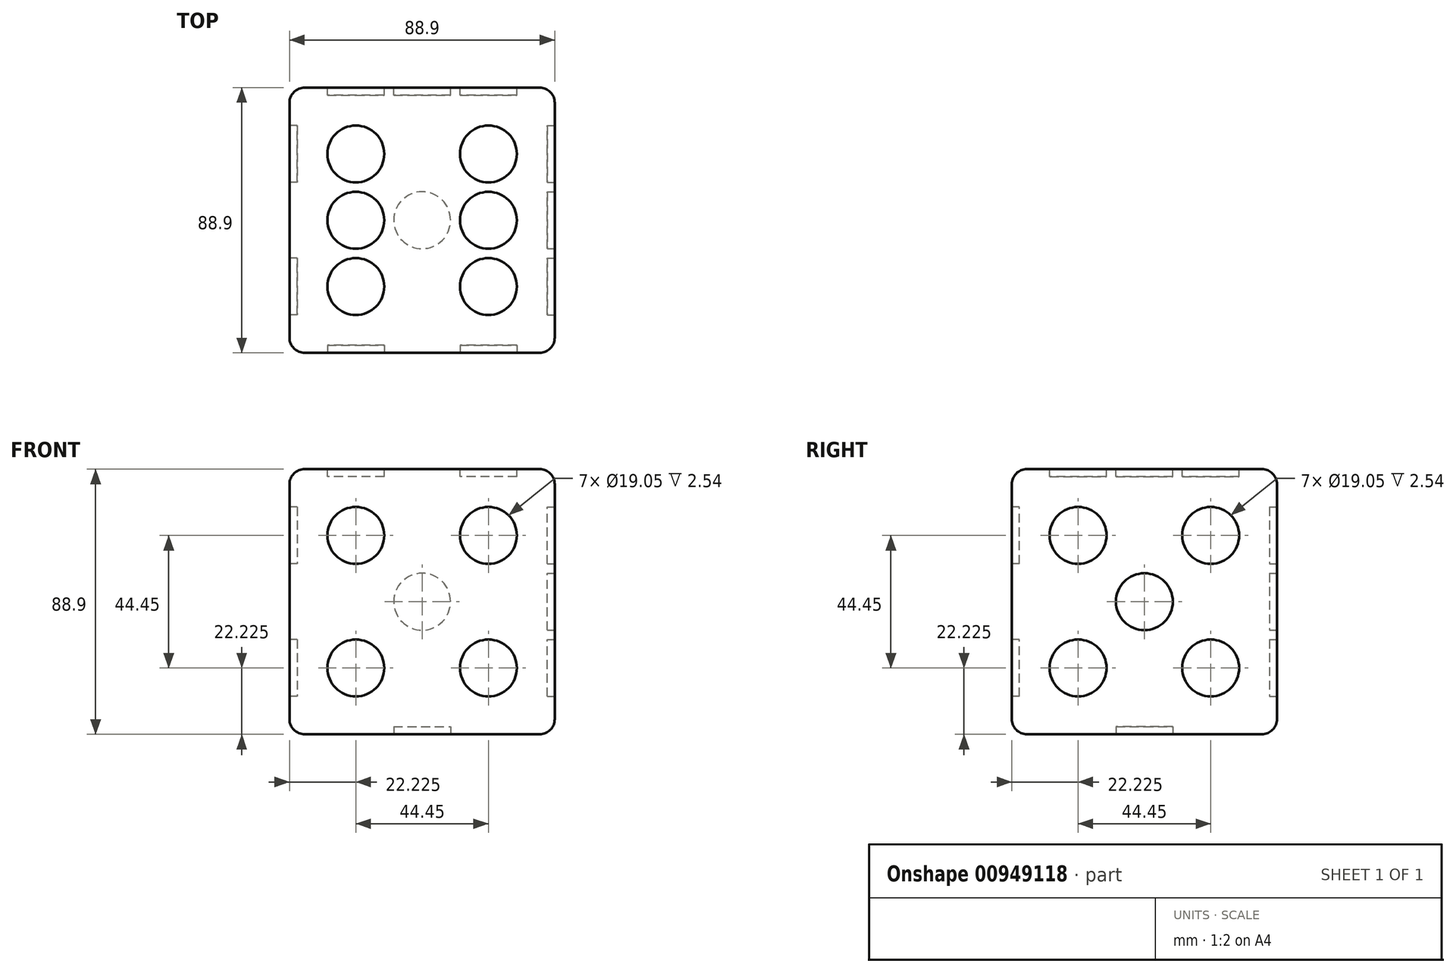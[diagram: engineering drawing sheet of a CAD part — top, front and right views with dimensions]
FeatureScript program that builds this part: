
annotation { "Feature Type Name" : "Feature", "Feature Type Description" : "" }
export const myFeature = defineFeature(function(context is Context, id is Id, definition is map)
    precondition{}
    {
        {
            var Q0;
            Q0=qCreatedBy(makeId("Top.planeOp"),FACE);
            var sketch = newSketch(context, id + "F0", { "sketchPlane" : qUnion([Q0])});
            skLineSegment(sketch, "E0.bottom", {"start": v(0, 0) * mm, "end": v(88.9, 0) * mm});
            skLineSegment(sketch, "E0.top", {"start": v(0, -88.9) * mm, "end": v(88.9, -88.9) * mm});
            skLineSegment(sketch, "E0.left", {"start": v(0, 0) * mm, "end": v(0, -88.9) * mm});
            skLineSegment(sketch, "E0.right", {"start": v(88.9, 0) * mm, "end": v(88.9, -88.9) * mm});
            skSolve(sketch);
        }
        {
            var Q0;
            Q0=makeQuery(id+"F0.imprint","IMPRINT",FACE,{"disambiguationData":[TD([[makeQuery(id+"F0.imprint","IMPRINT",EDGE,{"derivedFrom":sQuery(id+"F0.wireOp",EDGE,"E0.bottom")}),-1.0]])]});
            extrude(context, id + "F1", {"entities" : qUnion([Q0]), "flatOperationType" : FlatOperationType.REMOVE, "depth" : 88.9 * mm, "offsetDistance" : 25.4 * mm, "domain" : OperationDomain.MODEL});
        }
        {
            var Q0;
            Q0=makeQuery(id+"F1.opExtrude","CAP_FACE",FACE,{"disambiguationData":[OSD([sQuery(id+"F0.wireOp",EDGE,"E0.bottom"),sQuery(id+"F0.wireOp",EDGE,"E0.top"),sQuery(id+"F0.wireOp",EDGE,"E0.left"),sQuery(id+"F0.wireOp",EDGE,"E0.right")])],"isStart":false});
            var sketch = newSketch(context, id + "F2", { "sketchPlane" : qUnion([Q0])});
            skLineSegment(sketch, "E1.bottom", {"start": v(22.23, -22.22) * mm, "end": v(66.68, -22.22) * mm, "construction": true});
            skLineSegment(sketch, "E1.top", {"start": v(22.23, -66.67) * mm, "end": v(66.68, -66.67) * mm, "construction": true});
            skLineSegment(sketch, "E1.left", {"start": v(22.23, -22.22) * mm, "end": v(22.23, -66.67) * mm, "construction": true});
            skLineSegment(sketch, "E1.right", {"start": v(66.68, -22.22) * mm, "end": v(66.68, -66.67) * mm, "construction": true});
            skCircle(sketch, "E2", {"center": v(66.68, -22.22) * mm, "radius": 9.53 * mm});
            skCircle(sketch, "E3", {"center": v(22.23, -22.22) * mm, "radius": 9.53 * mm});
            skCircle(sketch, "E4", {"center": v(22.23, -66.67) * mm, "radius": 9.53 * mm});
            skCircle(sketch, "E5", {"center": v(66.68, -66.67) * mm, "radius": 9.53 * mm});
            skCircle(sketch, "E6", {"center": v(22.23, -44.45) * mm, "radius": 9.53 * mm});
            skCircle(sketch, "E7", {"center": v(66.68, -44.45) * mm, "radius": 9.53 * mm});
            skLineSegment(sketch, "E8", {"start": v(44.45, -22.22) * mm, "end": v(44.45, 0) * mm, "construction": true});
            skLineSegment(sketch, "E9", {"start": v(22.23, -44.45) * mm, "end": v(0, -44.45) * mm, "construction": true});
            skSolve(sketch);
        }
        {
            var Q0;
            Q0=makeQuery(id+"F2.imprint","IMPRINT",FACE,{"disambiguationData":[TD([[makeQuery(id+"F2.imprint","IMPRINT",EDGE,{"derivedFrom":sQuery(id+"F2.wireOp",EDGE,"E3")}),1.0]])]});
            var Q1;
            Q1=makeQuery(id+"F2.imprint","IMPRINT",FACE,{"disambiguationData":[TD([[makeQuery(id+"F2.imprint","IMPRINT",EDGE,{"derivedFrom":sQuery(id+"F2.wireOp",EDGE,"E2")}),1.0]])]});
            var Q2;
            Q2=makeQuery(id+"F2.imprint","IMPRINT",FACE,{"disambiguationData":[TD([[makeQuery(id+"F2.imprint","IMPRINT",EDGE,{"derivedFrom":sQuery(id+"F2.wireOp",EDGE,"E7")}),1.0]])]});
            var Q3;
            Q3=makeQuery(id+"F2.imprint","IMPRINT",FACE,{"disambiguationData":[TD([[makeQuery(id+"F2.imprint","IMPRINT",EDGE,{"derivedFrom":sQuery(id+"F2.wireOp",EDGE,"E6")}),1.0]])]});
            var Q4;
            Q4=makeQuery(id+"F2.imprint","IMPRINT",FACE,{"disambiguationData":[TD([[makeQuery(id+"F2.imprint","IMPRINT",EDGE,{"derivedFrom":sQuery(id+"F2.wireOp",EDGE,"E4")}),1.0]])]});
            var Q5;
            Q5=makeQuery(id+"F2.imprint","IMPRINT",FACE,{"disambiguationData":[TD([[makeQuery(id+"F2.imprint","IMPRINT",EDGE,{"derivedFrom":sQuery(id+"F2.wireOp",EDGE,"E5")}),1.0]])]});
            extrude(context, id + "F3", {"entities" : qUnion([Q0, Q1, Q2, Q3, Q4, Q5]), "operationType" : NewBodyOperationType.REMOVE, "oppositeDirection" : true, "depth" : 2.54 * mm, "offsetDistance" : 25.4 * mm});
        }
        {
            var Q0;
            Q0=makeQuery(id+"F1.opExtrude","SWEPT_FACE",FACE,{"disambiguationData":[OSD([sQuery(id+"F0.wireOp",EDGE,"E0.top")])]});
            var sketch = newSketch(context, id + "F4", { "sketchPlane" : qUnion([Q0])});
            skLineSegment(sketch, "E10.bottom", {"start": v(22.23, 66.67) * mm, "end": v(66.68, 66.67) * mm, "construction": true});
            skLineSegment(sketch, "E10.top", {"start": v(22.23, 22.23) * mm, "end": v(66.68, 22.23) * mm, "construction": true});
            skLineSegment(sketch, "E10.left", {"start": v(22.23, 66.68) * mm, "end": v(22.23, 22.22) * mm, "construction": true});
            skLineSegment(sketch, "E10.right", {"start": v(66.68, 66.68) * mm, "end": v(66.68, 22.22) * mm, "construction": true});
            skCircle(sketch, "E11", {"center": v(66.68, 66.68) * mm, "radius": 9.53 * mm});
            skCircle(sketch, "E12", {"center": v(66.68, 22.22) * mm, "radius": 9.53 * mm});
            skCircle(sketch, "E13", {"center": v(22.23, 22.22) * mm, "radius": 9.53 * mm});
            skCircle(sketch, "E14", {"center": v(22.23, 66.68) * mm, "radius": 9.53 * mm});
            skLineSegment(sketch, "E15", {"start": v(44.45, 66.67) * mm, "end": v(44.45, 88.9) * mm, "construction": true});
            skLineSegment(sketch, "E16", {"start": v(22.23, 44.45) * mm, "end": v(0, 44.45) * mm, "construction": true});
            skSolve(sketch);
        }
        {
            var Q0;
            Q0=makeQuery(id+"F4.imprint","IMPRINT",FACE,{"disambiguationData":[TD([[makeQuery(id+"F4.imprint","IMPRINT",EDGE,{"derivedFrom":sQuery(id+"F4.wireOp",EDGE,"E14")}),1.0]])]});
            var Q1;
            Q1=makeQuery(id+"F4.imprint","IMPRINT",FACE,{"disambiguationData":[TD([[makeQuery(id+"F4.imprint","IMPRINT",EDGE,{"derivedFrom":sQuery(id+"F4.wireOp",EDGE,"E11")}),1.0]])]});
            var Q2;
            Q2=makeQuery(id+"F4.imprint","IMPRINT",FACE,{"disambiguationData":[TD([[makeQuery(id+"F4.imprint","IMPRINT",EDGE,{"derivedFrom":sQuery(id+"F4.wireOp",EDGE,"E12")}),1.0]])]});
            var Q3;
            Q3=makeQuery(id+"F4.imprint","IMPRINT",FACE,{"disambiguationData":[TD([[makeQuery(id+"F4.imprint","IMPRINT",EDGE,{"derivedFrom":sQuery(id+"F4.wireOp",EDGE,"E13")}),1.0]])]});
            extrude(context, id + "F5", {"entities" : qUnion([Q0, Q1, Q2, Q3]), "operationType" : NewBodyOperationType.REMOVE, "oppositeDirection" : true, "depth" : 2.54 * mm, "offsetDistance" : 25.4 * mm});
        }
        {
            var Q0;
            Q0=makeQuery(id+"F1.opExtrude","CAP_FACE",FACE,{"disambiguationData":[OSD([sQuery(id+"F0.wireOp",EDGE,"E0.bottom"),sQuery(id+"F0.wireOp",EDGE,"E0.top"),sQuery(id+"F0.wireOp",EDGE,"E0.left"),sQuery(id+"F0.wireOp",EDGE,"E0.right")])],"isStart":true});
            var sketch = newSketch(context, id + "F6", { "sketchPlane" : qUnion([Q0])});
            skCircle(sketch, "E17", {"center": v(44.45, 44.45) * mm, "radius": 9.53 * mm});
            skLineSegment(sketch, "E18", {"start": v(44.45, 44.45) * mm, "end": v(0, 44.45) * mm, "construction": true});
            skLineSegment(sketch, "E19", {"start": v(44.45, 44.45) * mm, "end": v(44.45, 88.9) * mm, "construction": true});
            skSolve(sketch);
        }
        {
            var Q0;
            Q0=makeQuery(id+"F6.imprint","IMPRINT",FACE,{"disambiguationData":[TD([[makeQuery(id+"F6.imprint","IMPRINT",EDGE,{"derivedFrom":sQuery(id+"F6.wireOp",EDGE,"E17")}),1.0]])]});
            extrude(context, id + "F7", {"entities" : qUnion([Q0]), "operationType" : NewBodyOperationType.REMOVE, "oppositeDirection" : true, "depth" : 2.54 * mm, "offsetDistance" : 25.4 * mm});
        }
        {
            var Q0;
            Q0=makeQuery(id+"F1.opExtrude","SWEPT_FACE",FACE,{"disambiguationData":[OSD([sQuery(id+"F0.wireOp",EDGE,"E0.bottom")])]});
            var sketch = newSketch(context, id + "F8", { "sketchPlane" : qUnion([Q0])});
            skLineSegment(sketch, "E20.bottom", {"start": v(-66.67, 66.68) * mm, "end": v(-22.23, 66.68) * mm, "construction": true});
            skLineSegment(sketch, "E20.top", {"start": v(-66.67, 22.22) * mm, "end": v(-22.23, 22.22) * mm, "construction": true});
            skLineSegment(sketch, "E20.left", {"start": v(-66.67, 66.68) * mm, "end": v(-66.67, 22.22) * mm, "construction": true});
            skLineSegment(sketch, "E20.right", {"start": v(-22.22, 66.68) * mm, "end": v(-22.22, 22.22) * mm, "construction": true});
            skLineSegment(sketch, "E21", {"start": v(-66.67, 66.68) * mm, "end": v(-22.23, 22.22) * mm, "construction": true});
            skCircle(sketch, "E22", {"center": v(-66.67, 66.68) * mm, "radius": 9.53 * mm});
            skCircle(sketch, "E23", {"center": v(-44.45, 44.45) * mm, "radius": 9.53 * mm});
            skCircle(sketch, "E24", {"center": v(-22.23, 22.22) * mm, "radius": 9.53 * mm});
            skLineSegment(sketch, "E25", {"start": v(-66.67, 44.45) * mm, "end": v(-88.9, 44.45) * mm, "construction": true});
            skLineSegment(sketch, "E26", {"start": v(-44.45, 66.68) * mm, "end": v(-44.45, 88.9) * mm, "construction": true});
            skSolve(sketch);
        }
        {
            var Q0;
            Q0=makeQuery(id+"F8.imprint","IMPRINT",FACE,{"disambiguationData":[TD([[makeQuery(id+"F8.imprint","IMPRINT",EDGE,{"derivedFrom":sQuery(id+"F8.wireOp",EDGE,"E22")}),1.0]])]});
            var Q1;
            Q1=makeQuery(id+"F8.imprint","IMPRINT",FACE,{"disambiguationData":[TD([[makeQuery(id+"F8.imprint","IMPRINT",EDGE,{"derivedFrom":sQuery(id+"F8.wireOp",EDGE,"E23")}),1.0]])]});
            var Q2;
            Q2=makeQuery(id+"F8.imprint","IMPRINT",FACE,{"disambiguationData":[TD([[makeQuery(id+"F8.imprint","IMPRINT",EDGE,{"derivedFrom":sQuery(id+"F8.wireOp",EDGE,"E24")}),1.0]])]});
            var Q3;
            Q3=makeQuery(id+"F1.opExtrude","SWEPT_FACE",FACE,{"disambiguationData":[OSD([sQuery(id+"F0.wireOp",EDGE,"E0.top")])]});
            extrude(context, id + "F9", {"entities" : qUnion([Q0, Q1, Q2, Q3]), "operationType" : NewBodyOperationType.REMOVE, "oppositeDirection" : true, "depth" : 2.54 * mm, "offsetDistance" : 25.4 * mm});
        }
        {
            var Q0;
            Q0=makeQuery(id+"F1.opExtrude","SWEPT_FACE",FACE,{"disambiguationData":[OSD([sQuery(id+"F0.wireOp",EDGE,"E0.right")])]});
            var sketch = newSketch(context, id + "F10", { "sketchPlane" : qUnion([Q0])});
            skLineSegment(sketch, "E27.bottom", {"start": v(-66.67, 66.67) * mm, "end": v(-22.22, 66.67) * mm, "construction": true});
            skLineSegment(sketch, "E27.top", {"start": v(-66.67, 22.23) * mm, "end": v(-22.22, 22.23) * mm, "construction": true});
            skLineSegment(sketch, "E27.left", {"start": v(-66.67, 66.68) * mm, "end": v(-66.67, 22.23) * mm, "construction": true});
            skLineSegment(sketch, "E27.right", {"start": v(-22.22, 66.68) * mm, "end": v(-22.22, 22.23) * mm, "construction": true});
            skLineSegment(sketch, "E28", {"start": v(-66.68, 66.68) * mm, "end": v(-22.22, 22.22) * mm, "construction": true});
            skLineSegment(sketch, "E29", {"start": v(-66.67, 44.45) * mm, "end": v(-88.9, 44.45) * mm, "construction": true});
            skLineSegment(sketch, "E30", {"start": v(-44.45, 66.68) * mm, "end": v(-44.45, 88.9) * mm, "construction": true});
            skCircle(sketch, "E31", {"center": v(-66.67, 66.68) * mm, "radius": 9.53 * mm});
            skCircle(sketch, "E32", {"center": v(-66.67, 22.23) * mm, "radius": 9.53 * mm});
            skCircle(sketch, "E33", {"center": v(-22.22, 22.23) * mm, "radius": 9.53 * mm});
            skCircle(sketch, "E34", {"center": v(-22.22, 66.68) * mm, "radius": 9.53 * mm});
            skCircle(sketch, "E35", {"center": v(-44.45, 44.45) * mm, "radius": 9.53 * mm});
            skSolve(sketch);
        }
        {
            var Q0;
            Q0=makeQuery(id+"F10.imprint","IMPRINT",FACE,{"disambiguationData":[TD([[makeQuery(id+"F10.imprint","IMPRINT",EDGE,{"derivedFrom":sQuery(id+"F10.wireOp",EDGE,"E31")}),1.0]])]});
            var Q1;
            Q1=makeQuery(id+"F10.imprint","IMPRINT",FACE,{"disambiguationData":[TD([[makeQuery(id+"F10.imprint","IMPRINT",EDGE,{"derivedFrom":sQuery(id+"F10.wireOp",EDGE,"E34")}),1.0]])]});
            var Q2;
            Q2=makeQuery(id+"F10.imprint","IMPRINT",FACE,{"disambiguationData":[TD([[makeQuery(id+"F10.imprint","IMPRINT",EDGE,{"derivedFrom":sQuery(id+"F10.wireOp",EDGE,"E35")}),1.0]])]});
            var Q3;
            Q3=makeQuery(id+"F10.imprint","IMPRINT",FACE,{"disambiguationData":[TD([[makeQuery(id+"F10.imprint","IMPRINT",EDGE,{"derivedFrom":sQuery(id+"F10.wireOp",EDGE,"E32")}),1.0]])]});
            var Q4;
            Q4=makeQuery(id+"F10.imprint","IMPRINT",FACE,{"disambiguationData":[TD([[makeQuery(id+"F10.imprint","IMPRINT",EDGE,{"derivedFrom":sQuery(id+"F10.wireOp",EDGE,"E33")}),1.0]])]});
            extrude(context, id + "F11", {"entities" : qUnion([Q0, Q1, Q2, Q3, Q4]), "operationType" : NewBodyOperationType.REMOVE, "oppositeDirection" : true, "depth" : 2.54 * mm, "offsetDistance" : 25.4 * mm});
        }
        {
            var Q0;
            Q0=makeQuery(id+"F1.opExtrude","SWEPT_FACE",FACE,{"disambiguationData":[OSD([sQuery(id+"F0.wireOp",EDGE,"E0.left")])]});
            var sketch = newSketch(context, id + "F12", { "sketchPlane" : qUnion([Q0])});
            skLineSegment(sketch, "E36.bottom", {"start": v(22.22, 66.68) * mm, "end": v(66.67, 66.68) * mm, "construction": true});
            skLineSegment(sketch, "E36.top", {"start": v(22.22, 22.23) * mm, "end": v(66.67, 22.23) * mm, "construction": true});
            skLineSegment(sketch, "E36.left", {"start": v(22.23, 66.68) * mm, "end": v(22.23, 22.23) * mm, "construction": true});
            skLineSegment(sketch, "E36.right", {"start": v(66.68, 66.68) * mm, "end": v(66.68, 22.23) * mm, "construction": true});
            skLineSegment(sketch, "E37", {"start": v(22.23, 44.45) * mm, "end": v(0, 44.45) * mm, "construction": true});
            skLineSegment(sketch, "E38", {"start": v(44.45, 66.68) * mm, "end": v(44.45, 88.9) * mm, "construction": true});
            skCircle(sketch, "E39", {"center": v(22.22, 66.68) * mm, "radius": 9.53 * mm});
            skCircle(sketch, "E40", {"center": v(66.67, 22.23) * mm, "radius": 9.53 * mm});
            skSolve(sketch);
        }
        {
            var Q0;
            Q0=makeQuery(id+"F12.imprint","IMPRINT",FACE,{"disambiguationData":[TD([[makeQuery(id+"F12.imprint","IMPRINT",EDGE,{"derivedFrom":sQuery(id+"F12.wireOp",EDGE,"E39")}),1.0]])]});
            var Q1;
            Q1=makeQuery(id+"F12.imprint","IMPRINT",FACE,{"disambiguationData":[TD([[makeQuery(id+"F12.imprint","IMPRINT",EDGE,{"derivedFrom":sQuery(id+"F12.wireOp",EDGE,"E40")}),1.0]])]});
            extrude(context, id + "F13", {"entities" : qUnion([Q0, Q1]), "operationType" : NewBodyOperationType.REMOVE, "oppositeDirection" : true, "depth" : 2.54 * mm, "offsetDistance" : 25.4 * mm});
        }
        {
            var Q0;
            Q0=makeQuery(id+"F1.opExtrude","CAP_EDGE",EDGE,{"disambiguationData":[OSD([sQuery(id+"F0.wireOp",EDGE,"E0.left")])],"isStart":false});
            var Q1;
            Q1=makeQuery(id+"F1.opExtrude","CAP_EDGE",EDGE,{"disambiguationData":[OSD([sQuery(id+"F0.wireOp",EDGE,"E0.top")])],"isStart":false});
            var Q2;
            Q2=makeQuery(id+"F1.opExtrude","SWEPT_EDGE",EDGE,{"disambiguationData":[OSD([sQuery(id+"F0.wireOp",EDGE,"E0.top"),sQuery(id+"F0.wireOp",EDGE,"E0.left")])]});
            var Q3;
            Q3=makeQuery(id+"F1.opExtrude","CAP_EDGE",EDGE,{"disambiguationData":[OSD([sQuery(id+"F0.wireOp",EDGE,"E0.top")])],"isStart":true});
            var Q4;
            Q4=makeQuery(id+"F1.opExtrude","CAP_EDGE",EDGE,{"disambiguationData":[OSD([sQuery(id+"F0.wireOp",EDGE,"E0.left")])],"isStart":true});
            var Q5;
            Q5=makeQuery(id+"F1.opExtrude","CAP_EDGE",EDGE,{"disambiguationData":[OSD([sQuery(id+"F0.wireOp",EDGE,"E0.bottom")])],"isStart":true});
            var Q6;
            Q6=makeQuery(id+"F1.opExtrude","SWEPT_EDGE",EDGE,{"disambiguationData":[OSD([sQuery(id+"F0.wireOp",EDGE,"E0.bottom"),sQuery(id+"F0.wireOp",EDGE,"E0.left")])]});
            var Q7;
            Q7=makeQuery(id+"F1.opExtrude","CAP_EDGE",EDGE,{"disambiguationData":[OSD([sQuery(id+"F0.wireOp",EDGE,"E0.bottom")])],"isStart":false});
            var Q8;
            Q8=makeQuery(id+"F1.opExtrude","SWEPT_EDGE",EDGE,{"disambiguationData":[OSD([sQuery(id+"F0.wireOp",EDGE,"E0.bottom"),sQuery(id+"F0.wireOp",EDGE,"E0.right")])]});
            var Q9;
            Q9=makeQuery(id+"F1.opExtrude","CAP_EDGE",EDGE,{"disambiguationData":[OSD([sQuery(id+"F0.wireOp",EDGE,"E0.right")])],"isStart":false});
            var Q10;
            Q10=makeQuery(id+"F1.opExtrude","SWEPT_EDGE",EDGE,{"disambiguationData":[OSD([sQuery(id+"F0.wireOp",EDGE,"E0.top"),sQuery(id+"F0.wireOp",EDGE,"E0.right")])]});
            var Q11;
            Q11=makeQuery(id+"F1.opExtrude","CAP_EDGE",EDGE,{"disambiguationData":[OSD([sQuery(id+"F0.wireOp",EDGE,"E0.right")])],"isStart":true});
            fillet(context, id + "F14", {"entities" : qUnion([Q0, Q1, Q2, Q3, Q4, Q5, Q6, Q7, Q8, Q9, Q10, Q11]), "radius" : 5.08 * mm, "tangentPropagation" : true, "defaultsChanged" : false, "vertexSettings" : [], "allowEdgeOverflow" : false});
        }
    });
